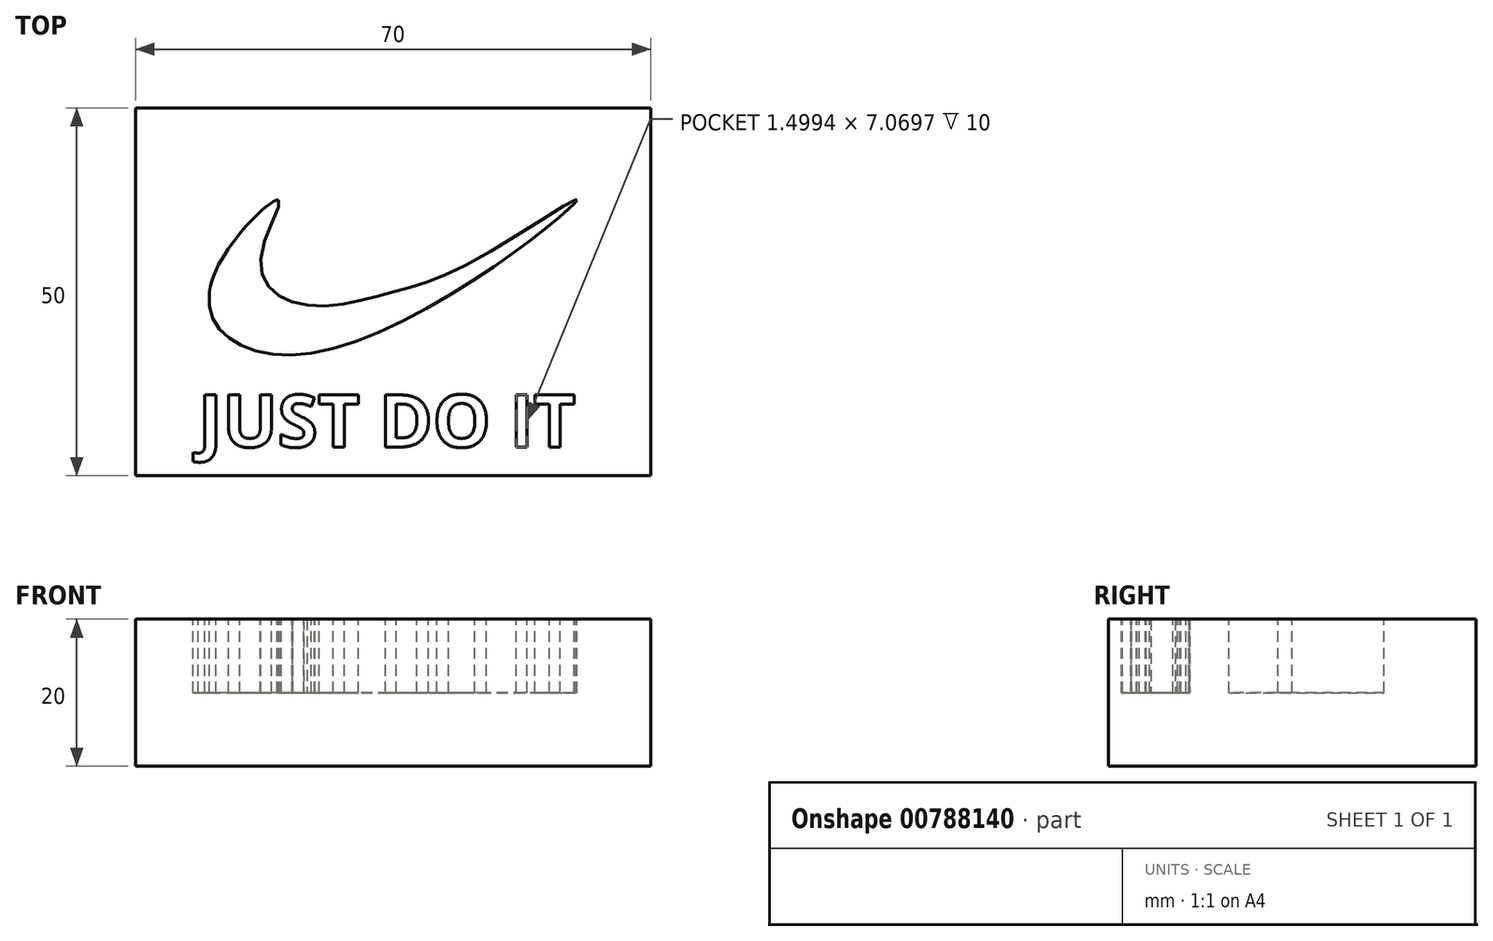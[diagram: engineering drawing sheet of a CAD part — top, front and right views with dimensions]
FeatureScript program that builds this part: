
annotation { "Feature Type Name" : "Feature", "Feature Type Description" : "" }
export const myFeature = defineFeature(function(context is Context, id is Id, definition is map)
    precondition{}
    {
        {
            var Q0;
            Q0=qCreatedBy(makeId("Top.planeOp"),FACE);
            var sketch = newSketch(context, id + "F0", { "sketchPlane" : qUnion([Q0])});
            skLineSegment(sketch, "E0.bottom", {"start": v(-35, 25) * mm, "end": v(35, 25) * mm});
            skLineSegment(sketch, "E0.top", {"start": v(-35, -25) * mm, "end": v(35, -25) * mm});
            skLineSegment(sketch, "E0.left", {"start": v(-35, 25) * mm, "end": v(-35, -25) * mm});
            skLineSegment(sketch, "E0.right", {"start": v(35, 25) * mm, "end": v(35, -25) * mm});
            skPoint(sketch, "E0.middle", {"position": v(0, 0) * mm});
            skSolve(sketch);
        }
        {
            var Q0;
            Q0=makeQuery(id+"F0.imprint","IMPRINT",FACE,{"disambiguationData":[TD([[makeQuery(id+"F0.imprint","IMPRINT",EDGE,{"derivedFrom":sQuery(id+"F0.wireOp",EDGE,"E0.bottom")}),-1.0]])]});
            var sketch = newSketch(context, id + "F1", { "sketchPlane" : qUnion([Q0])});
            skLineSegment(sketch, "E1.bottom", {"start": v(25, 12.5) * mm, "end": v(-25, 12.5) * mm});
            skLineSegment(sketch, "E1.top", {"start": v(25, -12.5) * mm, "end": v(-25, -12.5) * mm});
            skLineSegment(sketch, "E1.left", {"start": v(25, 12.5) * mm, "end": v(25, -12.5) * mm});
            skLineSegment(sketch, "E1.right", {"start": v(-25, 12.5) * mm, "end": v(-25, -12.5) * mm});
            skPoint(sketch, "E1.middle", {"position": v(0, 0) * mm});
            skSolve(sketch);
        }
        {
            var Q0;
            Q0=makeQuery(id+"F1.imprint","IMPRINT",FACE,{"disambiguationData":[TD([[makeQuery(id+"F1.imprint","IMPRINT",EDGE,{"derivedFrom":sQuery(id+"F1.wireOp",EDGE,"E1.bottom")}),1.0]])]});
            extrude(context, id + "F2", {"entities" : qUnion([Q0]), "depth" : 20 * mm, "offsetDistance" : 25 * mm});
        }
        {
            var Q0;
            Q0=makeQuery(id+"F2.opExtrude","CAP_FACE",FACE,{"disambiguationData":[OSD([sQuery(id+"F1.wireOp",EDGE,"E1.bottom"),sQuery(id+"F1.wireOp",EDGE,"E1.top"),sQuery(id+"F1.wireOp",EDGE,"E1.left"),sQuery(id+"F1.wireOp",EDGE,"E1.right")])],"isStart":false});
            var sketch = newSketch(context, id + "F3", { "sketchPlane" : qUnion([Q0])});
            skFitSpline(sketch, "E2", {"points": [v(-15.58, 12.5) * mm, v(-25, 0) * mm, v(-9.97, -8.14) * mm, v(25, 12.5) * mm, v(10.68, 4.04) * mm, v(0, 0) * mm, v(-9.36, -1.93) * mm, v(-16.22, 0) * mm, v(-17.78, 5.87) * mm, v(-15.58, 12.5) * mm]});
            skSolve(sketch);
        }
        {
            var Q0;
            Q0=makeQuery(id+"F0.imprint","IMPRINT",FACE,{"disambiguationData":[TD([[makeQuery(id+"F0.imprint","IMPRINT",EDGE,{"derivedFrom":sQuery(id+"F0.wireOp",EDGE,"E0.bottom")}),-1.0]])]});
            extrude(context, id + "F4", {"entities" : qUnion([Q0]), "operationType" : NewBodyOperationType.ADD, "depth" : 20 * mm, "offsetDistance" : 25 * mm});
        }
        {
            var Q0;
            {var subQ0=sQuery(id+"F3.wireOp",EDGE,"E2");var subQ2=makeQuery(id+"F2.opExtrude","CAP_EDGE",EDGE,{"disambiguationData":[OSD([sQuery(id+"F1.wireOp",EDGE,"E1.bottom")])],"isStart":false});var subQ9=makeQuery(id+"F3.imprint","INTERSECT",VERTEX,{"disambiguationData":[OD(0.0)],"derivedFrom":[subQ2,subQ0]});Q0=makeQuery(id+"F3.imprint","IMPRINT",FACE,{"disambiguationData":[TD([[makeQuery(id+"F3.imprint","IMPRINT",EDGE,{"disambiguationData":[TD([[subQ9,-1.0]])],"derivedFrom":subQ0}),1.0]])]});}
            extrude(context, id + "F5", {"entities" : qUnion([Q0]), "operationType" : NewBodyOperationType.REMOVE, "oppositeDirection" : true, "depth" : 10 * mm, "offsetDistance" : 25 * mm});
        }
        {
            var Q0;
            Q0=makeQuery(id+"F4.boolean.opBoolean","MERGE",FACE,{"derivedFrom":[makeQuery(id+"F2.opExtrude","CAP_FACE",FACE,{"disambiguationData":[OSD([sQuery(id+"F1.wireOp",EDGE,"E1.bottom"),sQuery(id+"F1.wireOp",EDGE,"E1.top"),sQuery(id+"F1.wireOp",EDGE,"E1.left"),sQuery(id+"F1.wireOp",EDGE,"E1.right")])],"isStart":false}),makeQuery(id+"F4.opExtrude","CAP_FACE",FACE,{"disambiguationData":[OSD([sQuery(id+"F0.wireOp",EDGE,"E0.bottom"),sQuery(id+"F0.wireOp",EDGE,"E0.top"),sQuery(id+"F0.wireOp",EDGE,"E0.left"),sQuery(id+"F0.wireOp",EDGE,"E0.right")])],"isStart":false})]});
            var sketch = newSketch(context, id + "F6", { "sketchPlane" : qUnion([Q0])});
            skText(sketch, "E3", { "text": "JUST DO IT", "fontName": "OpenSans-Bold.ttf"});
            const initialGuessF6  = {"E3": [-0.02648, -0.0211, 1, 0, 0.00713]};
            skSetInitialGuess(sketch, initialGuessF6);
            skSolve(sketch);
        }
        {
            var Q0;
            Q0=makeQuery(id+"F6.imprint","IMPRINT",FACE,{"disambiguationData":[TD([[makeQuery(id+"F6.imprint","IMPRINT",EDGE,{"derivedFrom":sQuery(id+"F6.wireOp",EDGE,"E3.sketch_text.stroke-25")}),-1.0]])]});
            var Q1;
            Q1=makeQuery(id+"F6.imprint","IMPRINT",FACE,{"disambiguationData":[TD([[makeQuery(id+"F6.imprint","IMPRINT",EDGE,{"derivedFrom":sQuery(id+"F6.wireOp",EDGE,"E3.sketch_text.stroke-53")}),-1.0]])]});
            var Q2;
            Q2=makeQuery(id+"F6.imprint","IMPRINT",FACE,{"disambiguationData":[TD([[makeQuery(id+"F6.imprint","IMPRINT",EDGE,{"derivedFrom":sQuery(id+"F6.wireOp",EDGE,"E3.sketch_text.stroke-61")}),-1.0]])]});
            var Q3;
            Q3=makeQuery(id+"F6.imprint","IMPRINT",FACE,{"disambiguationData":[TD([[makeQuery(id+"F6.imprint","IMPRINT",EDGE,{"derivedFrom":sQuery(id+"F6.wireOp",EDGE,"E3.sketch_text.stroke-73")}),-1.0]])]});
            var Q4;
            Q4=makeQuery(id+"F6.imprint","IMPRINT",FACE,{"disambiguationData":[TD([[makeQuery(id+"F6.imprint","IMPRINT",EDGE,{"derivedFrom":sQuery(id+"F6.wireOp",EDGE,"E3.sketch_text.stroke-87")}),-1.0]])]});
            var Q5;
            Q5=makeQuery(id+"F6.imprint","IMPRINT",FACE,{"disambiguationData":[TD([[makeQuery(id+"F6.imprint","IMPRINT",EDGE,{"derivedFrom":sQuery(id+"F6.wireOp",EDGE,"E3.sketch_text.stroke-91")}),-1.0]])]});
            var Q6;
            Q6=makeQuery(id+"F6.imprint","IMPRINT",FACE,{"disambiguationData":[TD([[makeQuery(id+"F6.imprint","IMPRINT",EDGE,{"derivedFrom":sQuery(id+"F6.wireOp",EDGE,"E3.sketch_text.stroke-10")}),-1.0]])]});
            var Q7;
            Q7=makeQuery(id+"F6.imprint","IMPRINT",FACE,{"disambiguationData":[TD([[makeQuery(id+"F6.imprint","IMPRINT",EDGE,{"derivedFrom":sQuery(id+"F6.wireOp",EDGE,"E3.sketch_text.stroke-0")}),-1.0]])]});
            var Q8;
            Q8 = qConstructionFilter(qBodyType(qCreatedBy(id + "F6" ,EDGE), BodyType.WIRE), ConstructionObject.NO);
            extrude(context, id + "F7", {"entities" : qUnion([Q0, Q1, Q2, Q3, Q4, Q5, Q6, Q7]), "operationType" : NewBodyOperationType.REMOVE, "surfaceEntities" : qUnion([Q8]), "oppositeDirection" : true, "depth" : 10 * mm, "offsetDistance" : 25 * mm});
        }
    });
